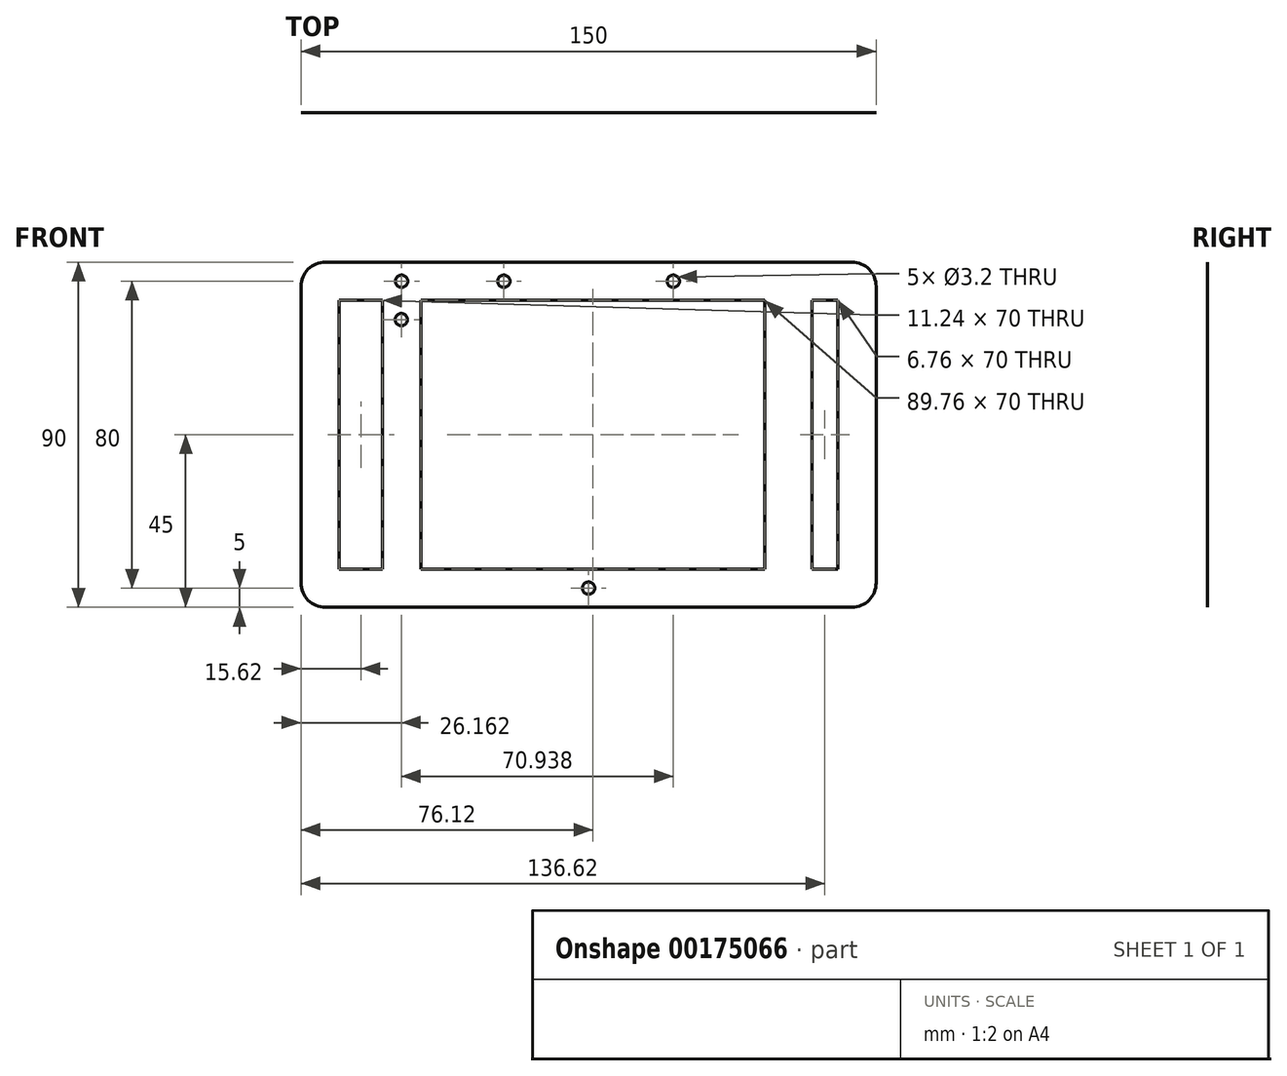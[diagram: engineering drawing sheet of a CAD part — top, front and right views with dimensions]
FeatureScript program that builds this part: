
annotation { "Feature Type Name" : "Feature", "Feature Type Description" : "" }
export const myFeature = defineFeature(function(context is Context, id is Id, definition is map)
    precondition{}
    {
        {
            var Q0;
            Q0=qCreatedBy(makeId("Front.planeOp"),FACE);
            var sketch = newSketch(context, id + "F0", { "sketchPlane" : qUnion([Q0])});
            skLineSegment(sketch, "E0.bottom", {"start": v(6.35, 0) * mm, "end": v(143.65, 0) * mm});
            skLineSegment(sketch, "E0.top", {"start": v(6.35, -90) * mm, "end": v(143.65, -90) * mm});
            skLineSegment(sketch, "E0.left", {"start": v(0, -6.35) * mm, "end": v(0, -83.65) * mm});
            skLineSegment(sketch, "E0.right", {"start": v(150, -6.35) * mm, "end": v(150, -83.65) * mm});
            skLineSegment(sketch, "E1.bottom", {"start": v(10, -10) * mm, "end": v(21.24, -10) * mm});
            skLineSegment(sketch, "E1.top", {"start": v(10, -80) * mm, "end": v(21.24, -80) * mm});
            skLineSegment(sketch, "E1.left", {"start": v(10, -10) * mm, "end": v(10, -80) * mm});
            skLineSegment(sketch, "E1.right", {"start": v(140, -10) * mm, "end": v(140, -80) * mm});
            skCircle(sketch, "E2", {"center": v(75, -85) * mm, "radius": 1.6 * mm});
            skPoint(sketch, "E2.centerSnap0", {"position": v(75, -90) * mm});
            skCircle(sketch, "E3", {"center": v(52.9, -5) * mm, "radius": 1.6 * mm});
            skCircle(sketch, "E4", {"center": v(97.1, -5) * mm, "radius": 1.6 * mm});
            skPoint(sketch, "E5.endSnap0", {"position": v(75, -10) * mm});
            skLineSegment(sketch, "E6.bottom", {"start": v(21.24, 0) * mm, "end": v(31.24, 0) * mm});
            skLineSegment(sketch, "E6.top", {"start": v(21.24, -90) * mm, "end": v(31.24, -90) * mm});
            skLineSegment(sketch, "E6.left", {"start": v(21.24, -10) * mm, "end": v(21.24, -80) * mm});
            skLineSegment(sketch, "E6.right", {"start": v(31.24, -10) * mm, "end": v(31.24, -80) * mm});
            skLineSegment(sketch, "E7.MirrorCS", {"start": v(121, -10) * mm, "end": v(121, -80) * mm});
            skLineSegment(sketch, "E8.MirrorCS", {"start": v(133.24, -10) * mm, "end": v(133.24, -80) * mm});
            skLineSegment(sketch, "E9.trimOffspring", {"start": v(31.24, -10) * mm, "end": v(121, -10) * mm});
            skLineSegment(sketch, "E10.trimOffspring", {"start": v(31.24, -80) * mm, "end": v(121, -80) * mm});
            skLineSegment(sketch, "E11.trimOffspring", {"start": v(133.24, -80) * mm, "end": v(140, -80) * mm});
            skLineSegment(sketch, "E12.trimOffspring", {"start": v(133.24, -10) * mm, "end": v(140, -10) * mm});
            skPoint(sketch, "E13.end.orphan", {"position": v(136.62, -80) * mm});
            skPoint(sketch, "E13.start.orphan", {"position": v(136.62, -10) * mm});
            skPoint(sketch, "E14.visualSharp", {"position": v(0, 0) * mm});
            skArc(sketch, "E14.filletArc", {"start": v(6.35, 0) * mm, "mid": v(1.86, -1.86) * mm, "end": v(0, -6.35) * mm});
            skPoint(sketch, "E15.visualSharp", {"position": v(0, -90) * mm});
            skArc(sketch, "E15.filletArc", {"start": v(0, -83.65) * mm, "mid": v(1.86, -88.14) * mm, "end": v(6.35, -90) * mm});
            skPoint(sketch, "E16.visualSharp", {"position": v(150, -90) * mm});
            skArc(sketch, "E16.filletArc", {"start": v(143.65, -90) * mm, "mid": v(148.14, -88.14) * mm, "end": v(150, -83.65) * mm});
            skPoint(sketch, "E17.visualSharp", {"position": v(150, 0) * mm});
            skArc(sketch, "E17.filletArc", {"start": v(150, -6.35) * mm, "mid": v(148.14, -1.86) * mm, "end": v(143.65, 0) * mm});
            skCircle(sketch, "E18", {"center": v(26.24, -5) * mm, "radius": 1.6 * mm});
            skPoint(sketch, "E18.centerSnap0", {"position": v(26.24, 0) * mm});
            skCircle(sketch, "E19.0.1.0", {"center": v(26.16, -14.99) * mm, "radius": 1.6 * mm});
            skLineSegment(sketch, "E19.direction1", {"start": v(26.24, -5) * mm, "end": v(50.88, -5) * mm, "construction": true});
            skLineSegment(sketch, "E19.direction2", {"start": v(26.24, -5) * mm, "end": v(26.16, -14.99) * mm, "construction": true});
            skSolve(sketch);
        }
        {
            var Q0;
            Q0=makeQuery(id+"F0.imprint","IMPRINT",FACE,{"disambiguationData":[TD([[makeQuery(id+"F0.imprint","IMPRINT",EDGE,{"derivedFrom":sQuery(id+"F0.wireOp",EDGE,"E0.bottom")}),-1.0]])]});
            extrude(context, id + "F1", {"entities" : qUnion([Q0]), "depth" : 1 / 203.2 * mm});
        }
    });
